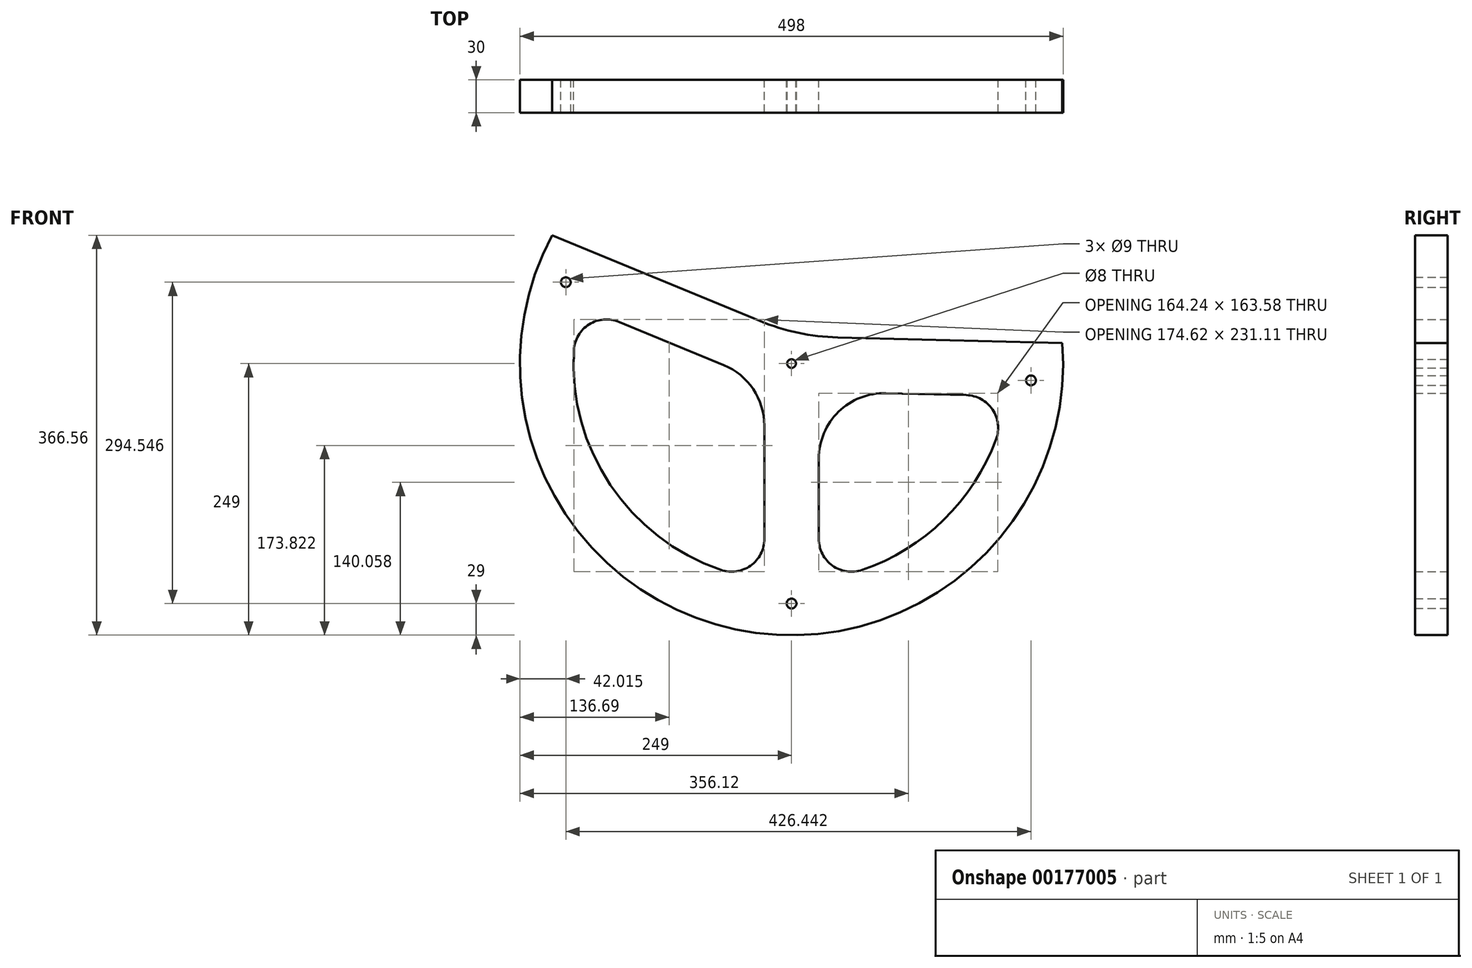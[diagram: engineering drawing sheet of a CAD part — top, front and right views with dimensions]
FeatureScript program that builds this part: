
annotation { "Feature Type Name" : "Feature", "Feature Type Description" : "" }
export const myFeature = defineFeature(function(context is Context, id is Id, definition is map)
    precondition{}
    {
        {
            var Q0;
            Q0=qCreatedBy(makeId("Front.planeOp"),FACE);
            var sketch = newSketch(context, id + "F0", { "sketchPlane" : qUnion([Q0])});
            skArc(sketch, "E0", {"start": v(-219.5, 117.56) * mm, "mid": v(-51.41, -243.63) * mm, "end": v(248.29, 18.85) * mm});
            skLineSegment(sketch, "E1", {"start": v(0, 272.01) * mm, "end": v(0, -280.99) * mm, "construction": true});
            skCircle(sketch, "E2", {"center": v(0, 0) * mm, "radius": 220 * mm, "construction": true});
            skCircle(sketch, "E3", {"center": v(0, -220) * mm, "radius": 4.5 * mm});
            skCircle(sketch, "E4", {"center": v(219.46, -15.45) * mm, "radius": 4.5 * mm});
            skCircle(sketch, "E5", {"center": v(-206.99, 74.55) * mm, "radius": 4.5 * mm});
            skArc(sketch, "E6", {"start": v(-199.62, 12.33) * mm, "mid": v(-166.2, -111.24) * mm, "end": v(-64.7, -189.24) * mm});
            skCircle(sketch, "E7", {"center": v(0, 0) * mm, "radius": 4 * mm});
            skLineSegment(sketch, "E8", {"start": v(25, -87.13) * mm, "end": v(25, -160.86) * mm});
            skLineSegment(sketch, "E9", {"start": v(-25, -160.86) * mm, "end": v(-25, -56.9) * mm});
            skPoint(sketch, "E10", {"position": v(-203.38, 83.87) * mm});
            skPoint(sketch, "E11", {"position": v(219.93, -5.45) * mm});
            skLineSegment(sketch, "E12", {"start": v(0, 0) * mm, "end": v(219.93, -5.45) * mm, "construction": true});
            skLineSegment(sketch, "E13", {"start": v(0, 0) * mm, "end": v(-203.38, 83.87) * mm, "construction": true});
            skLineSegment(sketch, "E14", {"start": v(-219.5, 117.56) * mm, "end": v(-29, 39) * mm});
            skLineSegment(sketch, "E15", {"start": v(42.29, 23.96) * mm, "end": v(248.29, 18.85) * mm});
            skLineSegment(sketch, "E16", {"start": v(86.49, -27.15) * mm, "end": v(160.19, -28.98) * mm});
            skLineSegment(sketch, "E17.trimOffspring", {"start": v(-62.13, -1.42) * mm, "end": v(-158.24, 38.21) * mm});
            skArc(sketch, "E18.trimOffspring", {"start": v(64.7, -189.24) * mm, "mid": v(139.66, -143.16) * mm, "end": v(187.58, -69.38) * mm});
            skPoint(sketch, "E19.visualSharp", {"position": v(-192.98, 52.54) * mm});
            skArc(sketch, "E19.filletArc", {"start": v(-158.24, 38.21) * mm, "mid": v(-185.59, 35.91) * mm, "end": v(-199.62, 12.33) * mm});
            skPoint(sketch, "E20.visualSharp", {"position": v(-25, -198.43) * mm});
            skArc(sketch, "E20.filletArc", {"start": v(-64.7, -189.24) * mm, "mid": v(-37.55, -185.26) * mm, "end": v(-25, -160.86) * mm});
            skPoint(sketch, "E21.visualSharp", {"position": v(25, -198.43) * mm});
            skArc(sketch, "E21.filletArc", {"start": v(25, -160.86) * mm, "mid": v(37.55, -185.26) * mm, "end": v(64.7, -189.24) * mm});
            skPoint(sketch, "E22.visualSharp", {"position": v(197.75, -29.91) * mm});
            skArc(sketch, "E22.filletArc", {"start": v(187.58, -69.38) * mm, "mid": v(184.27, -42.13) * mm, "end": v(160.19, -28.98) * mm});
            skPoint(sketch, "E23.visualSharp", {"position": v(25, -25.63) * mm});
            skArc(sketch, "E23.filletArc", {"start": v(86.49, -27.15) * mm, "mid": v(43.1, -44.19) * mm, "end": v(25, -87.13) * mm});
            skPoint(sketch, "E24.visualSharp", {"position": v(-25, -16.73) * mm});
            skArc(sketch, "E24.filletArc", {"start": v(-25, -56.9) * mm, "mid": v(-35.14, -23.52) * mm, "end": v(-62.13, -1.42) * mm});
            skPoint(sketch, "E25.visualSharp", {"position": v(5.25, 24.88) * mm});
            skArc(sketch, "E25.filletArc", {"start": v(-29, 39) * mm, "mid": v(5.95, 28.2) * mm, "end": v(42.29, 23.96) * mm});
            skSolve(sketch);
        }
        {
            var Q0;
            Q0=makeQuery(id+"F0.imprint","IMPRINT",FACE,{"disambiguationData":[TD([[makeQuery(id+"F0.imprint","IMPRINT",EDGE,{"derivedFrom":sQuery(id+"F0.wireOp",EDGE,"E0")}),1.0]])]});
            extrude(context, id + "F1", {"entities" : qUnion([Q0]), "depth" : 30 * mm});
        }
    });
